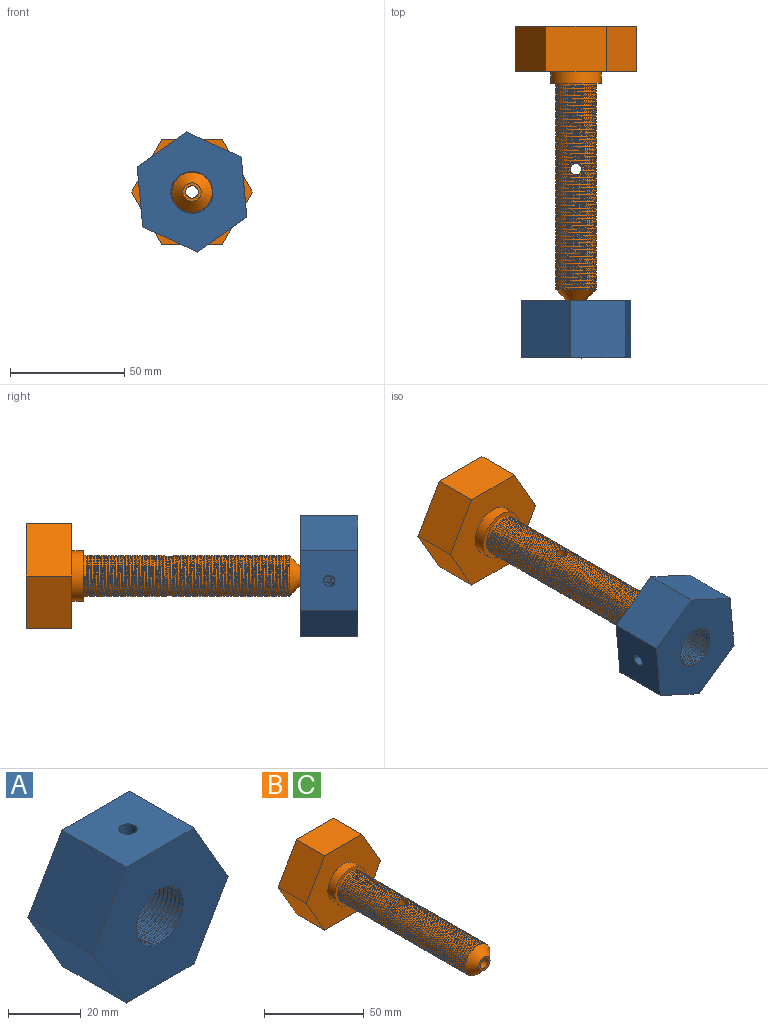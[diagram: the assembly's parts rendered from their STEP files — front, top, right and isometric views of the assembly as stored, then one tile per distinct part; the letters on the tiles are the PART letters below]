
ASSEMBLY  parts=3 mates=1
PART A: 38 faces, bbox 52.9x26.3x45.9 mm
  f0: cylinder r=9mm len=17.37mm, axis (0,1,0), area 17mm2, adj f8,f24,f36,f37
  f1: cylinder r=9mm len=17.56mm, axis (0,1,0), area 17.4mm2, adj f10,f26,f36,f37
  f2: cylinder r=9mm len=18mm, axis (0,1,0), area 292.1mm2, adj f11,f12,f27,f35,f36,f37
  f3: cylinder r=9mm len=17.36mm, axis (0,1,0), area 17mm2, adj f9,f25,f36,f37
  f4: cylinder r=9mm len=17.56mm, axis (0,1,0), area 17.4mm2, adj f7,f23,f36,f37
  f5: cylinder r=9mm len=18mm, axis (0,1,0), area 301.1mm2, adj f6,f21,f22,f34,f36,f37
  f6: bspline ~21.5x18.62mm, area 174mm2, adj f5,f19,f34,f36
  f7: bspline ~21.5x13.97mm, area 11mm2, adj f4,f13,f36,f37
  f8: bspline ~21.5x13.97mm, area 10.5mm2, adj f0,f18,f36,f37
  f9: bspline ~21.5x13.97mm, area 10.4mm2, adj f3,f14,f36,f37
  f10: bspline ~21.5x13.97mm, area 10.4mm2, adj f1,f17,f36,f37
  f11: bspline ~21.5x13.97mm, area 10.7mm2, adj f2,f15,f36,f37
  f12: bspline ~21.5x18.62mm, area 177.6mm2, adj f2,f16,f20,f35,f36,f37
  f13: cylinder r=9.31mm len=18.38mm, axis (0,1,0), area 4.2mm2, adj f7,f21,f36,f37
  f14: cylinder r=9.31mm len=17.97mm, axis (0,1,0), area 3.9mm2, adj f9,f23,f36,f37
  f15: cylinder r=9.31mm len=18.11mm, axis (0,1,0), area 3.9mm2, adj f11,f25,f36,f37
  f16: cylinder r=9.31mm len=18.37mm, axis (0,1,0), area 4.1mm2, adj f12,f26,f36,f37
  f17: cylinder r=9.31mm len=17.97mm, axis (0,1,0), area 3.9mm2, adj f10,f24,f36,f37
  f18: cylinder r=9.31mm len=18.11mm, axis (0,1,0), area 3.9mm2, adj f8,f22,f36,f37
  f19: cylinder r=9.31mm len=18.62mm, axis (0,1,0), area 53.9mm2, adj f6,f21,f34,f36
  f20: cylinder r=9.31mm len=18.62mm, axis (0,1,0), area 129.6mm2, adj f12,f27,f35,f36
  f21: bspline ~21.5x18.62mm, area 179.4mm2, adj f5,f13,f19,f34,f36,f37
  f22: bspline ~21.5x13.97mm, area 10.8mm2, adj f5,f18,f36,f37
  f23: bspline ~21.5x13.97mm, area 10.4mm2, adj f4,f14,f36,f37
  f24: bspline ~21.5x13.97mm, area 10.4mm2, adj f0,f17,f36,f37
  f25: bspline ~21.5x13.97mm, area 10.5mm2, adj f3,f15,f36,f37
  f26: bspline ~21.5x13.97mm, area 11mm2, adj f1,f16,f36,f37
  f27: bspline ~21.5x18.62mm, area 175.4mm2, adj f2,f20,f35,f36
  f28: plane 25x22.84mm, normal (-0.87,0,0.5), area 659.4mm2, adj f29,f33,f34,f35
  f29: plane 25x22.84mm, normal (-0.87,0,-0.5), area 659.4mm2, adj f28,f30,f34,f35
  f30: plane 26.38x25mm, normal (0,0,-1), area 639.8mm2, adj f29,f31,f34,f35,f36
  f31: plane 25x22.84mm, normal (0.87,0,-0.5), area 659.4mm2, adj f30,f32,f34,f35
  f32: plane 25x22.84mm, normal (0.87,0,0.5), area 659.4mm2, adj f31,f33,f34,f35
  f33: plane 26.38x25mm, normal (0,0,1), area 639.8mm2, adj f28,f32,f34,f35,f37
  f34: plane 52.94x45.88mm, normal (0,-1,0), area 1547.6mm2, adj f5,f6,f19,f21,f28,f29,f30,f31
  f35: plane 52.94x45.88mm, normal (0,1,0), area 1547.6mm2, adj f2,f12,f20,f27,f28,f29,f30,f31
  f36: cylinder r=2.5mm len=14.2mm, axis (0,0,-1), area 218.1mm2, adj f0,f1,f2,f3,f4,f5,f6,f7
  f37: cylinder r=2.5mm len=14.19mm, axis (0,0,-1), area 219.1mm2, adj f0,f1,f2,f3,f4,f5,f7,f8
PART B: 44 faces, bbox 52.8x120x45.7 mm
  f0: cylinder r=2.5mm len=7.86mm, axis (0,0,-1), area 105.7mm2, adj f2,f3,f4,f5,f6,f7,f8,f9
  f1: cylinder r=2.5mm len=7.73mm, axis (0,0,-1), area 104.6mm2, adj f2,f3,f4,f5,f6,f7,f8,f9
  f2: cylinder r=9mm len=17.37mm, axis (0,1,0), area 17mm2, adj f0,f1,f11,f25
  f3: cylinder r=9mm len=17.56mm, axis (0,1,0), area 17.4mm2, adj f0,f1,f13,f27
  f4: cylinder r=9mm len=36.31mm, axis (0,1,0), area 1002.7mm2, adj f0,f1,f14,f28,f29,f40,f42
  f5: cylinder r=9mm len=17.36mm, axis (0,1,0), area 17mm2, adj f0,f1,f12,f26
  f6: cylinder r=9mm len=17.56mm, axis (0,1,0), area 17.4mm2, adj f0,f1,f10,f24
  f7: cylinder r=9mm len=51.29mm, axis (0,1,0), area 1600.7mm2, adj f0,f1,f8,f9,f23,f30
  f8: bspline ~51.81x20.78mm, area 823.4mm2, adj f0,f1,f7,f20,f22,f30
  f9: bspline ~20.78x13.5mm, area 10.3mm2, adj f0,f1,f7,f15
  f10: bspline ~20.78x13.5mm, area 10mm2, adj f0,f1,f6,f19
  f11: bspline ~20.78x13.5mm, area 9.9mm2, adj f0,f1,f2,f16
  f12: bspline ~20.78x13.5mm, area 10.1mm2, adj f0,f1,f5,f18
  f13: bspline ~20.78x13.5mm, area 10.5mm2, adj f0,f1,f3,f17
  f14: bspline ~35.31x20.78mm, area 563.9mm2, adj f1,f4,f21,f42
  f15: cylinder r=8.69mm len=16.83mm, axis (0,1,0), area 3.6mm2, adj f0,f1,f9,f25
  f16: cylinder r=8.69mm len=16.68mm, axis (0,1,0), area 3.5mm2, adj f0,f1,f11,f27
  f17: cylinder r=8.69mm len=17.11mm, axis (0,1,0), area 3.8mm2, adj f0,f1,f13,f29
  f18: cylinder r=8.69mm len=16.83mm, axis (0,1,0), area 3.6mm2, adj f0,f1,f12,f28
  f19: cylinder r=8.69mm len=16.68mm, axis (0,1,0), area 3.5mm2, adj f0,f1,f10,f26
  f20: cylinder r=8.69mm len=17.12mm, axis (0,1,0), area 3.8mm2, adj f0,f1,f8,f24
  f21: cylinder r=8.69mm len=35mm, axis (0,1,0), area 219.6mm2, adj f1,f14,f29,f42
  f22: cylinder r=8.69mm len=50.6mm, axis (0,1,0), area -356.8mm2, adj f1,f8,f23,f30
  f23: bspline ~50.9x17.99mm, area 819.8mm2, adj f1,f7,f22,f30
  f24: bspline ~20.78x13.5mm, area 10.6mm2, adj f0,f1,f6,f20
  f25: bspline ~20.78x13.5mm, area 10.1mm2, adj f0,f1,f2,f15
  f26: bspline ~20.78x13.5mm, area 9.9mm2, adj f0,f1,f5,f19
  f27: bspline ~20.78x13.5mm, area 10mm2, adj f0,f1,f3,f16
  f28: bspline ~20.78x13.5mm, area 10.3mm2, adj f0,f1,f4,f18
  f29: bspline ~36.06x20.78mm, area 575.2mm2, adj f0,f1,f4,f17,f21,f42
  f30: cone r=4mm half-angle=45deg, axis (0,1,0), area 281.1mm2, adj f7,f8,f22,f23,f41
  f31: plane 22.84x20mm, normal (-0.87,0,0.5), area 527.5mm2, adj f32,f36,f37,f38
  f32: plane 22.84x20mm, normal (-0.87,0,-0.5), area 527.5mm2, adj f31,f33,f37,f38
  f33: plane 26.38x20mm, normal (0,0,-1), area 527.5mm2, adj f32,f34,f37,f38
  f34: plane 22.84x20mm, normal (0.87,0,-0.5), area 527.5mm2, adj f33,f35,f37,f38
  f35: plane 22.84x20mm, normal (0.87,0,0.5), area 527.5mm2, adj f34,f36,f37,f38
  f36: plane 26.38x20mm, normal (0,0,1), area 527.5mm2, adj f31,f35,f37,f38
  f37: plane 52.75x45.69mm, normal (0,-1,0), area 1427.4mm2, adj f31,f32,f33,f34,f35,f36,f39
  f38: plane 52.75x45.69mm, normal (0,1,0), area 1783.8mm2, adj f31,f32,f33,f34,f35,f36,f43
  f39: cylinder r=11mm len=22mm, axis (0,1,0), area 345.6mm2, adj f37,f40
  f40: plane 22x22mm, normal (0,-1,0), area 125.7mm2, adj f4,f39
  f41: plane 8x8mm, normal (0,-1,0), area 26.5mm2, adj f30,f43
  f42: plane 0.77x0.31mm, normal (0,0,-1), area 0.1mm2, adj f4,f14,f21,f29
  f43: cylinder r=2.75mm len=120mm, axis (0,1,0), area 2031.3mm2, adj f0,f1,f38,f41
PART C: same geometry as B
PLACE A rot(axis=(0.74,0,-0.67),180deg) t=(15.06,-195,16.52)mm
PLACE B at identity
PLACE C at identity fixed
MATE revolute A.f0 <-> C.f2  axis (0,-1,0) through (0,-120,15.12)mm
